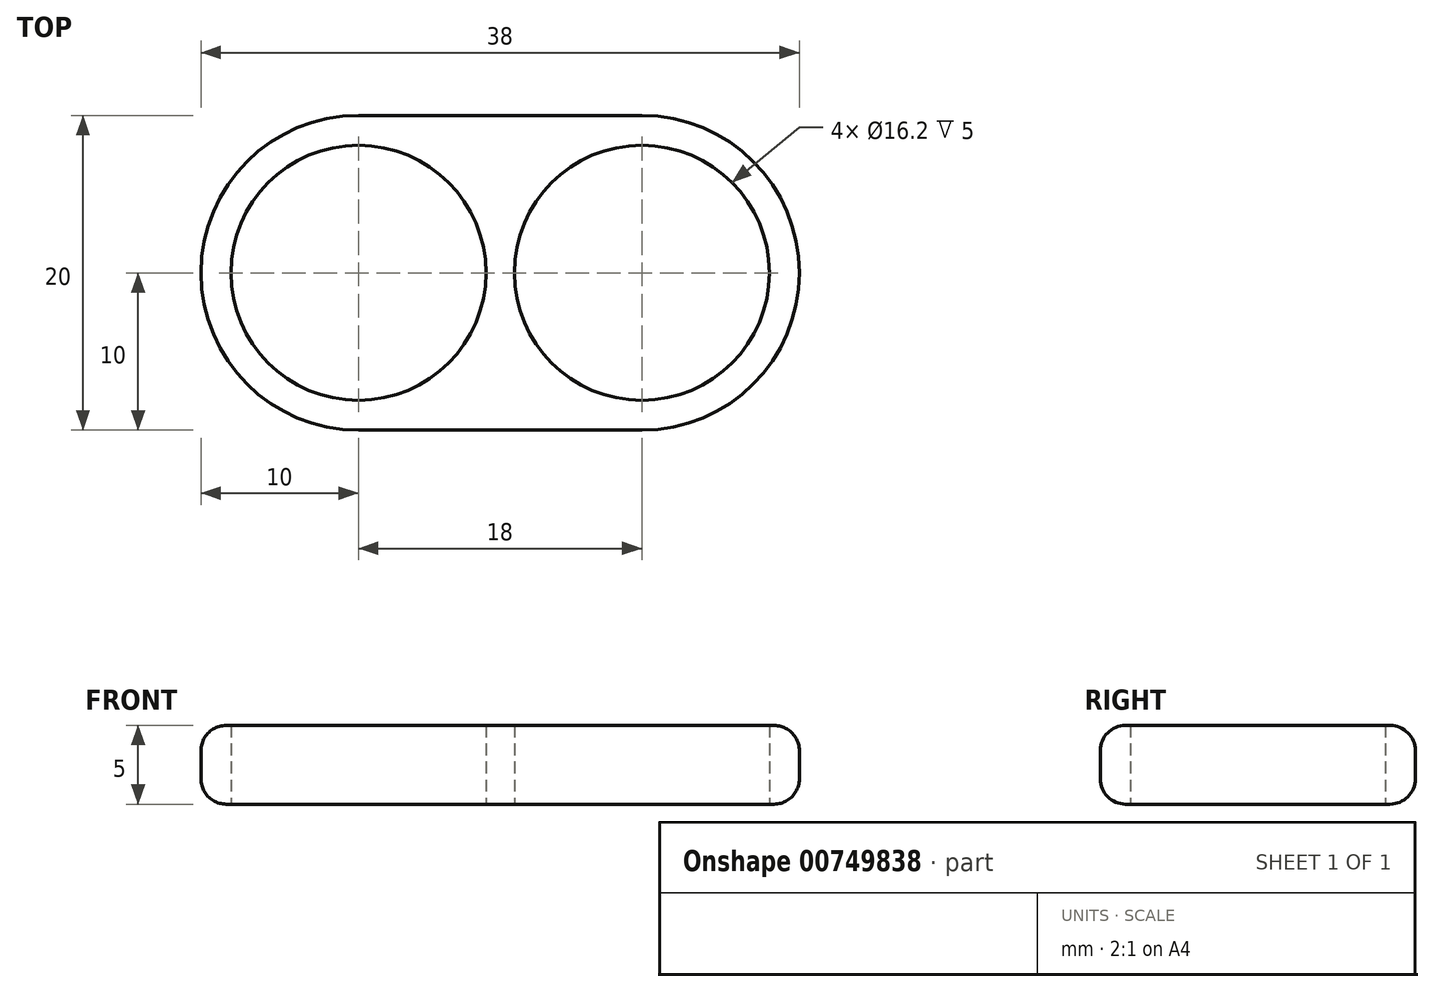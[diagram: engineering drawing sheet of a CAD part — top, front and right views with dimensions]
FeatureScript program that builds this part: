
annotation { "Feature Type Name" : "Feature", "Feature Type Description" : "" }
export const myFeature = defineFeature(function(context is Context, id is Id, definition is map)
    precondition{}
    {
        {
            var Q0;
            Q0=qCreatedBy(makeId("Top.planeOp"),FACE);
            var sketch = newSketch(context, id + "F0", { "sketchPlane" : qUnion([Q0])});
            skCircle(sketch, "E0", {"center": v(-9, 0) * mm, "radius": 8.1 * mm});
            skCircle(sketch, "E1", {"center": v(9, 0) * mm, "radius": 8.1 * mm});
            skLineSegment(sketch, "E2", {"start": v(-9, 10) * mm, "end": v(9, 10) * mm});
            skLineSegment(sketch, "E3", {"start": v(-9, -10) * mm, "end": v(9, -10) * mm});
            skArc(sketch, "E4", {"start": v(-9, 10) * mm, "mid": v(-19, 0) * mm, "end": v(-9, -10) * mm});
            skArc(sketch, "E5", {"start": v(9, 10) * mm, "mid": v(19, 0) * mm, "end": v(9, -10) * mm});
            skSolve(sketch);
        }
        {
            var Q0;
            Q0=makeQuery(id+"F0.imprint","IMPRINT",FACE,{"disambiguationData":[TD([[makeQuery(id+"F0.imprint","IMPRINT",EDGE,{"derivedFrom":sQuery(id+"F0.wireOp",EDGE,"E0")}),-1.0]])]});
            extrude(context, id + "F1", {"entities" : qUnion([Q0]), "depth" : 5 * mm, "offsetDistance" : 25 * mm});
        }
        {
            var Q0;
            Q0=makeQuery(id+"F1.opExtrude","SWEPT_FACE",FACE,{"disambiguationData":[OSD([sQuery(id+"F0.wireOp",EDGE,"E3")])]});
            var Q1;
            Q1=makeQuery(id+"F1.opExtrude","SWEPT_FACE",FACE,{"disambiguationData":[OSD([sQuery(id+"F0.wireOp",EDGE,"E5")])]});
            fillet(context, id + "F2", {"entities" : qUnion([Q0, Q1]), "radius" : 1.6 * mm, "tangentPropagation" : true, "allowEdgeOverflow" : false});
        }
    });
